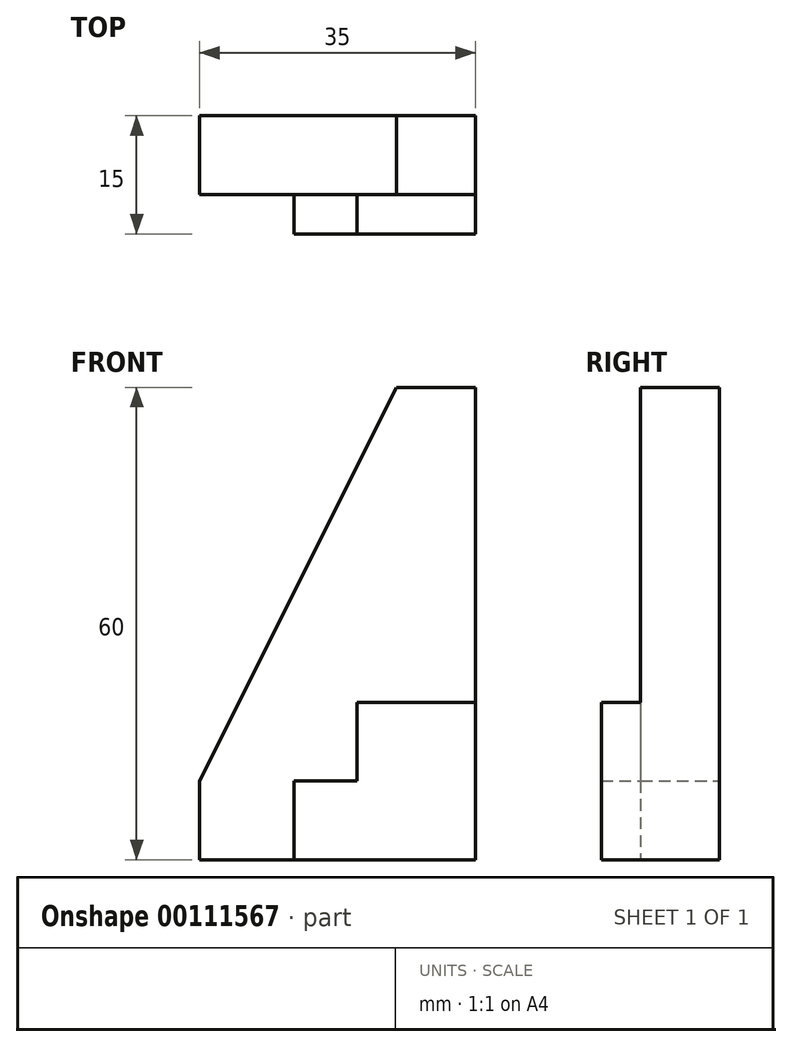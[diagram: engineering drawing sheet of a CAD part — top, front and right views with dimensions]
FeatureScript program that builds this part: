
annotation { "Feature Type Name" : "Feature", "Feature Type Description" : "" }
export const myFeature = defineFeature(function(context is Context, id is Id, definition is map)
    precondition{}
    {
        {
            var Q0;
            Q0=qCreatedBy(makeId("Front.planeOp"),FACE);
            var sketch = newSketch(context, id + "F0", { "sketchPlane" : qUnion([Q0])});
            skLineSegment(sketch, "E0", {"start": v(-19.1, 0) * mm, "end": v(-19.1, 60) * mm});
            skLineSegment(sketch, "E1", {"start": v(-19.1, 60) * mm, "end": v(-29.1, 60) * mm});
            skLineSegment(sketch, "E2", {"start": v(-29.1, 60) * mm, "end": v(-54.1, 10) * mm});
            skLineSegment(sketch, "E3", {"start": v(-54.1, 10) * mm, "end": v(-54.1, 0) * mm});
            skLineSegment(sketch, "E4", {"start": v(-54.1, 0) * mm, "end": v(-19.1, 0) * mm});
            skSolve(sketch);
        }
        {
            var Q0;
            Q0=qSketchRegion(id+"F0",true);
            var Q1;
            Q1=makeQuery(id+"F0.imprint","IMPRINT",FACE,{"disambiguationData":[TD([[makeQuery(id+"F0.imprint","IMPRINT",EDGE,{"derivedFrom":sQuery(id+"F0.wireOp",EDGE,"E0")}),1.0]])]});
            extrude(context, id + "F1", {"entities" : qUnion([Q0, Q1]), "depth" : 10 * mm});
        }
        {
            var Q0;
            Q0=makeQuery(id+"F1.opExtrude","CAP_FACE",FACE,{"disambiguationData":[OSD([sQuery(id+"F0.wireOp",EDGE,"E0"),sQuery(id+"F0.wireOp",EDGE,"E1"),sQuery(id+"F0.wireOp",EDGE,"E2"),sQuery(id+"F0.wireOp",EDGE,"E3"),sQuery(id+"F0.wireOp",EDGE,"E4")])],"isStart":false});
            var sketch = newSketch(context, id + "F2", { "sketchPlane" : qUnion([Q0])});
            skLineSegment(sketch, "E5", {"start": v(-19.1, 20) * mm, "end": v(-34.1, 20) * mm});
            skLineSegment(sketch, "E6", {"start": v(-34.1, 20) * mm, "end": v(-34.1, 10) * mm});
            skLineSegment(sketch, "E7", {"start": v(-34.1, 10) * mm, "end": v(-42.1, 10) * mm});
            skLineSegment(sketch, "E8", {"start": v(-42.1, 10) * mm, "end": v(-42.1, 0) * mm});
            skSolve(sketch);
        }
        {
            var Q0;
            {var subQ4=sQuery(id+"F2.wireOp",EDGE,"E5");Q0=makeQuery(id+"F2.imprint","IMPRINT",FACE,{"disambiguationData":[TD([[makeQuery(id+"F2.imprint","IMPRINT",EDGE,{"derivedFrom":subQ4}),1.0]])]});}
            extrude(context, id + "F3", {"entities" : qUnion([Q0]), "operationType" : NewBodyOperationType.ADD, "depth" : 5 * mm});
        }
    });
